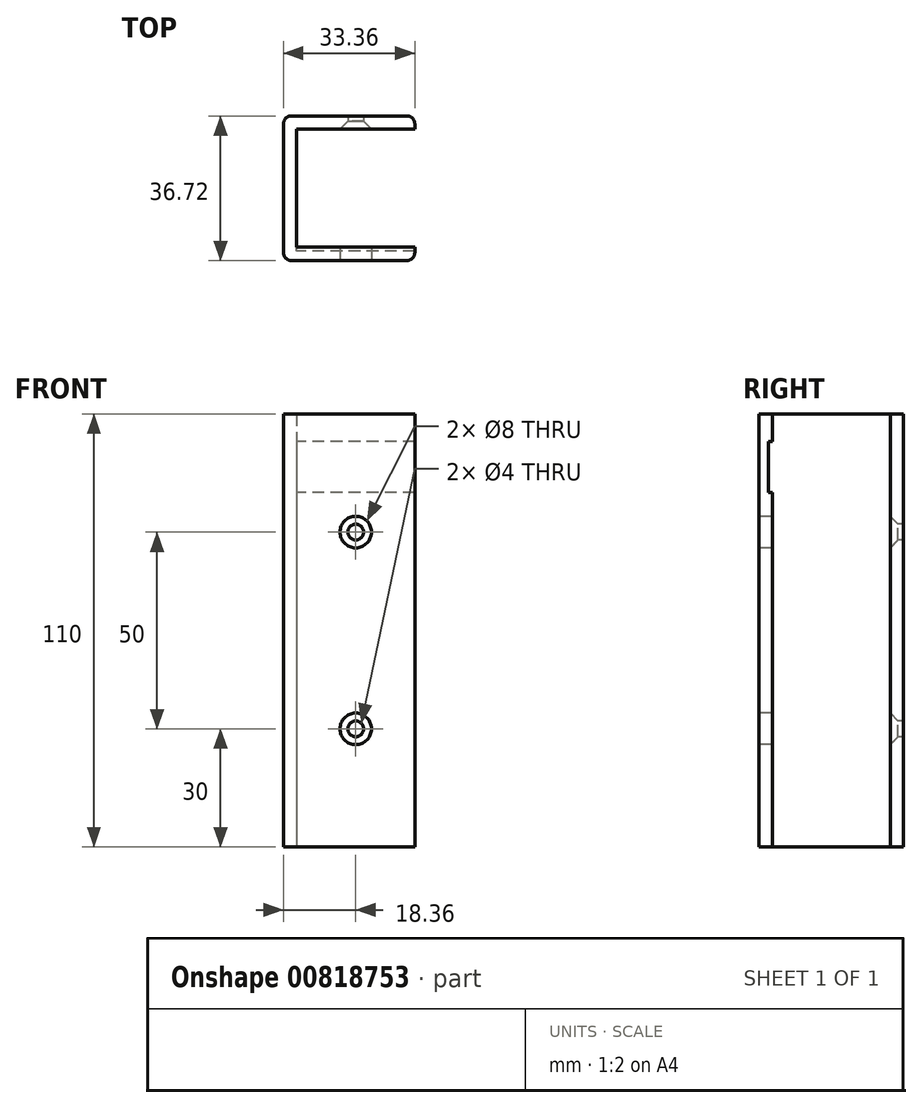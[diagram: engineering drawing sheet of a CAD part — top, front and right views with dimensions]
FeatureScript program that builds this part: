
annotation { "Feature Type Name" : "Feature", "Feature Type Description" : "" }
export const myFeature = defineFeature(function(context is Context, id is Id, definition is map)
    precondition{}
    {
        {
            var Q0;
            Q0=qCreatedBy(makeId("Top.planeOp"),FACE);
            var sketch = newSketch(context, id + "F0", { "sketchPlane" : qUnion([Q0])});
            skLineSegment(sketch, "E0.bottom", {"start": v(15, -15) * mm, "end": v(-15, -15) * mm});
            skLineSegment(sketch, "E0.top", {"start": v(15, 15) * mm, "end": v(-15, 15) * mm});
            skLineSegment(sketch, "E0.left", {"start": v(15, -15) * mm, "end": v(15, 15) * mm});
            skLineSegment(sketch, "E0.right", {"start": v(-15, -15) * mm, "end": v(-15, 15) * mm});
            skPoint(sketch, "E0.middle", {"position": v(0, 0) * mm});
            skLineSegment(sketch, "E1", {"start": v(15, 15) * mm, "end": v(15, 18.36) * mm});
            skLineSegment(sketch, "E2", {"start": v(-18.36, 18.36) * mm, "end": v(15, 18.36) * mm});
            skLineSegment(sketch, "E3", {"start": v(15, 0) * mm, "end": v(-15, 0) * mm, "construction": true});
            skLineSegment(sketch, "E4.MirrorCS", {"start": v(-18.36, -18.36) * mm, "end": v(15, -18.36) * mm});
            skLineSegment(sketch, "E5", {"start": v(15, -15) * mm, "end": v(15, -18.36) * mm});
            skLineSegment(sketch, "E6", {"start": v(-18.36, 18.36) * mm, "end": v(-18.36, -18.36) * mm});
            skSolve(sketch);
        }
        {
            var Q0;
            Q0=makeQuery(id+"F0.imprint","IMPRINT",FACE,{"disambiguationData":[TD([[makeQuery(id+"F0.imprint","IMPRINT",EDGE,{"derivedFrom":sQuery(id+"F0.wireOp",EDGE,"E0.bottom")}),1.0]])]});
            extrude(context, id + "F1", {"entities" : qUnion([Q0]), "depth" : 110 * mm, "offsetDistance" : 25 * mm});
        }
        {
            var Q0;
            Q0=makeQuery(id+"F1.opExtrude","SWEPT_EDGE",EDGE,{"disambiguationData":[OSD([sQuery(id+"F0.wireOp",EDGE,"E4.MirrorCS"),sQuery(id+"F0.wireOp",EDGE,"E6")])]});
            var Q1;
            Q1=makeQuery(id+"F1.opExtrude","SWEPT_EDGE",EDGE,{"disambiguationData":[OSD([sQuery(id+"F0.wireOp",EDGE,"E2"),sQuery(id+"F0.wireOp",EDGE,"E6")])]});
            var Q2;
            Q2=makeQuery(id+"F1.opExtrude","SWEPT_EDGE",EDGE,{"disambiguationData":[OSD([sQuery(id+"F0.wireOp",EDGE,"E4.MirrorCS"),sQuery(id+"F0.wireOp",EDGE,"E5")])]});
            var Q3;
            Q3=makeQuery(id+"F1.opExtrude","SWEPT_EDGE",EDGE,{"disambiguationData":[OSD([sQuery(id+"F0.wireOp",EDGE,"E1"),sQuery(id+"F0.wireOp",EDGE,"E2")])]});
            fillet(context, id + "F2", {"entities" : qUnion([Q0, Q1, Q2, Q3]), "radius" : 2 * mm, "tangentPropagation" : true, "allowEdgeOverflow" : false});
        }
        {
            var Q0;
            Q0=makeQuery(id+"F1.opExtrude","SWEPT_FACE",FACE,{"disambiguationData":[OSD([sQuery(id+"F0.wireOp",EDGE,"E4.MirrorCS")])]});
            var sketch = newSketch(context, id + "F3", { "sketchPlane" : qUnion([Q0])});
            skPoint(sketch, "E7", {"position": v(0, 30) * mm});
            skPoint(sketch, "E8", {"position": v(0, 80) * mm});
            skSolve(sketch);
        }
        {
            var Q0;
            Q0=sQuery(id+"F3.wireOp",VERTEX,"E7");
            var Q1;
            Q1=sQuery(id+"F3.wireOp",VERTEX,"E8");
            var Q2;
            Q2=makeQuery(id+"F1.opExtrude","SWEPT_BODY",BODY,{"disambiguationData":[OSD([sQuery(id+"F0.wireOp",EDGE,"E0.bottom"),sQuery(id+"F0.wireOp",EDGE,"E0.top"),sQuery(id+"F0.wireOp",EDGE,"E0.right"),sQuery(id+"F0.wireOp",EDGE,"E1"),sQuery(id+"F0.wireOp",EDGE,"E2"),sQuery(id+"F0.wireOp",EDGE,"E4.MirrorCS"),sQuery(id+"F0.wireOp",EDGE,"E5"),sQuery(id+"F0.wireOp",EDGE,"E6")])]});
            hole(context, id + "F4", {"style" : HoleStyle.SIMPLE, "endStyle" : HoleEndStyle.BLIND, "holeDiameter" : 8 * mm, "majorDiameter" : 5 * mm, "holeDepth" : 4 * mm, "isTappedThrough" : true, "tappedDepth" : 12 * mm, "tapClearance" : 3, "startFromSketch" : true, "locations" : qUnion([Q0, Q1]), "scope" : qUnion([Q2])});
        }
        {
            var Q0;
            Q0=makeQuery(id+"F1.opExtrude","SWEPT_FACE",FACE,{"disambiguationData":[OSD([sQuery(id+"F0.wireOp",EDGE,"E0.top")])]});
            var sketch = newSketch(context, id + "F5", { "sketchPlane" : qUnion([Q0])});
            skPoint(sketch, "E9", {"position": v(0, 30) * mm});
            skLineSegment(sketch, "E10", {"start": v(15, 55) * mm, "end": v(-15, 55) * mm, "construction": true});
            skPoint(sketch, "E11", {"position": v(0, 80) * mm});
            skPoint(sketch, "E11.positionSnap0", {"position": v(0, 55) * mm});
            skSolve(sketch);
        }
        {
            var Q0;
            Q0=sQuery(id+"F5.wireOp",VERTEX,"E9");
            var Q1;
            Q1=sQuery(id+"F5.wireOp",VERTEX,"E11");
            var Q2;
            Q2=makeQuery(id+"F1.opExtrude","SWEPT_BODY",BODY,{"disambiguationData":[OSD([sQuery(id+"F0.wireOp",EDGE,"E0.bottom"),sQuery(id+"F0.wireOp",EDGE,"E0.top"),sQuery(id+"F0.wireOp",EDGE,"E0.right"),sQuery(id+"F0.wireOp",EDGE,"E1"),sQuery(id+"F0.wireOp",EDGE,"E2"),sQuery(id+"F0.wireOp",EDGE,"E4.MirrorCS"),sQuery(id+"F0.wireOp",EDGE,"E5"),sQuery(id+"F0.wireOp",EDGE,"E6")])]});
            hole(context, id + "F6", {"style" : HoleStyle.C_SINK, "endStyle" : HoleEndStyle.BLIND, "holeDiameter" : 4 * mm, "cSinkDiameter" : 8 * mm, "cSinkAngle" : 90 * degree, "majorDiameter" : 5 * mm, "holeDepth" : 4 * mm, "isTappedThrough" : true, "tappedDepth" : 12 * mm, "tapClearance" : 3, "startFromSketch" : true, "locations" : qUnion([Q0, Q1]), "scope" : qUnion([Q2])});
        }
        {
            var Q0;
            Q0=makeQuery(id+"F1.opExtrude","SWEPT_FACE",FACE,{"disambiguationData":[OSD([sQuery(id+"F0.wireOp",EDGE,"E0.bottom")])]});
            var sketch = newSketch(context, id + "F7", { "sketchPlane" : qUnion([Q0])});
            skLineSegment(sketch, "E12.bottom", {"start": v(15, 110) * mm, "end": v(-15, 110) * mm, "construction": true});
            skLineSegment(sketch, "E12.top", {"start": v(15, 103) * mm, "end": v(-15, 103) * mm, "construction": true});
            skLineSegment(sketch, "E12.left", {"start": v(15, 110) * mm, "end": v(15, 103) * mm, "construction": true});
            skLineSegment(sketch, "E12.right", {"start": v(-15, 110) * mm, "end": v(-15, 103) * mm, "construction": true});
            skLineSegment(sketch, "E13.bottom", {"start": v(-15, 103) * mm, "end": v(15, 103) * mm});
            skLineSegment(sketch, "E13.top", {"start": v(-15, 90) * mm, "end": v(15, 90) * mm});
            skLineSegment(sketch, "E13.left", {"start": v(-15, 103) * mm, "end": v(-15, 90) * mm});
            skLineSegment(sketch, "E13.right", {"start": v(15, 103) * mm, "end": v(15, 90) * mm});
            skSolve(sketch);
        }
        {
            var Q0;
            Q0=makeQuery(id+"F7.imprint","IMPRINT",FACE,{"disambiguationData":[TD([[makeQuery(id+"F7.imprint","IMPRINT",EDGE,{"derivedFrom":sQuery(id+"F7.wireOp",EDGE,"E13.bottom")}),-1.0]])]});
            extrude(context, id + "F8", {"entities" : qUnion([Q0]), "operationType" : NewBodyOperationType.REMOVE, "oppositeDirection" : true, "depth" : 1 * mm, "offsetDistance" : 25 * mm});
        }
    });
